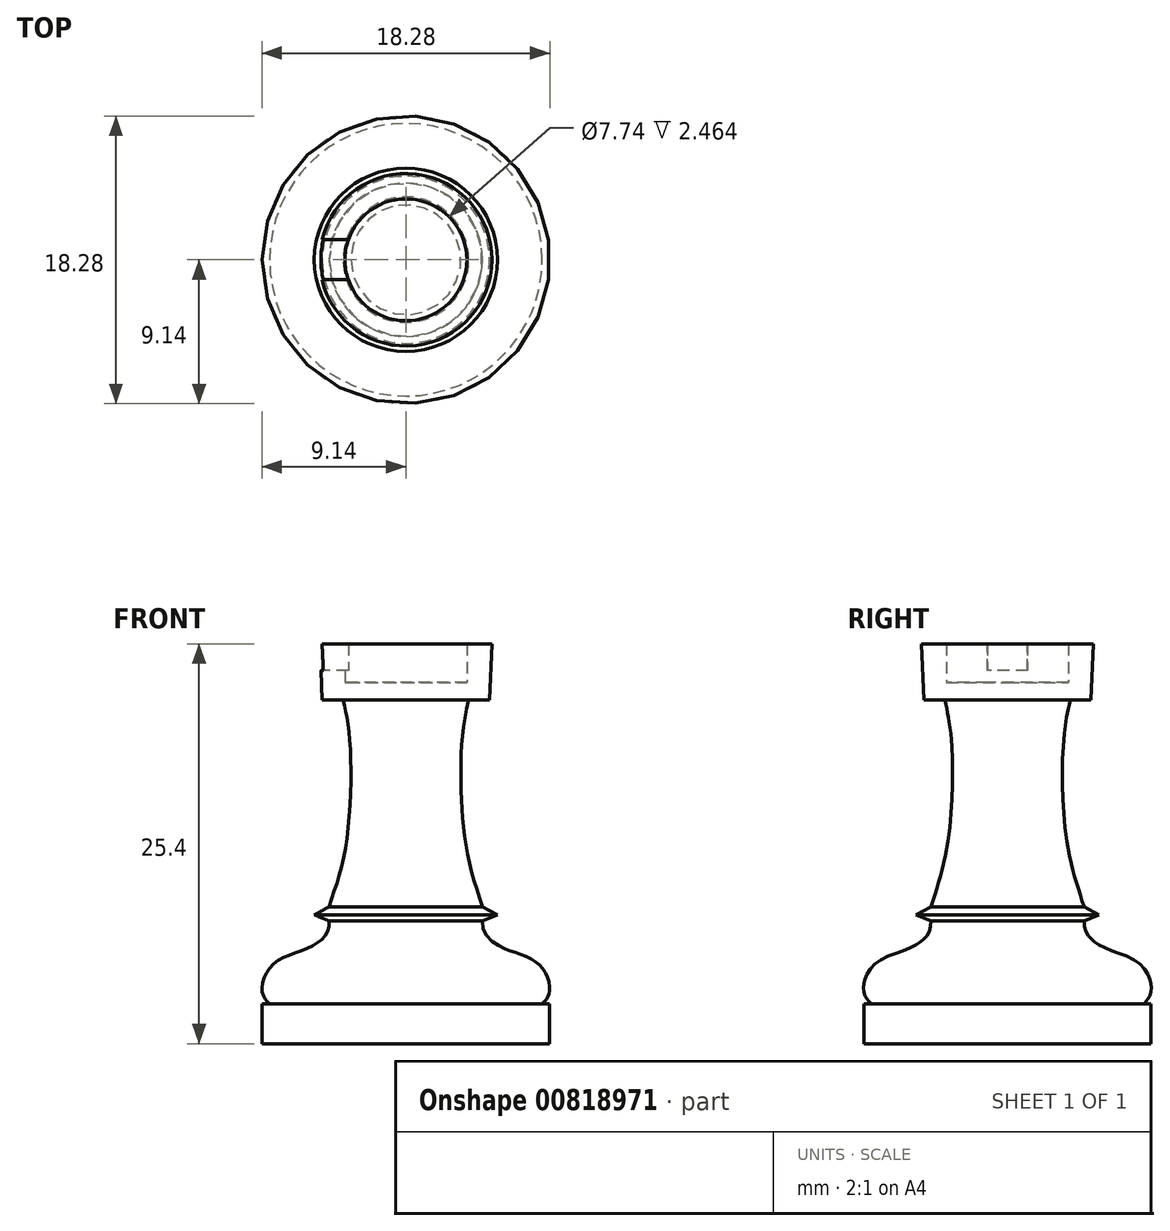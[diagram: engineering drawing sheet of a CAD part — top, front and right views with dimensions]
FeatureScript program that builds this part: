
annotation { "Feature Type Name" : "Feature", "Feature Type Description" : "" }
export const myFeature = defineFeature(function(context is Context, id is Id, definition is map)
    precondition{}
    {
        {
            var Q0;
            Q0=qCreatedBy(makeId("Front.planeOp"),FACE);
            var sketch = newSketch(context, id + "F0", { "sketchPlane" : qUnion([Q0])});
            skLineSegment(sketch, "E0", {"start": v(0, 0) * mm, "end": v(9.12, 0) * mm});
            skLineSegment(sketch, "E1", {"start": v(0, 0) * mm, "end": v(0, 25.4) * mm});
            skLineSegment(sketch, "E2", {"start": v(9.12, 0) * mm, "end": v(9.12, 2.54) * mm});
            skLineSegment(sketch, "E3", {"start": v(9.12, 2.54) * mm, "end": v(0, 2.54) * mm});
            skPoint(sketch, "E4.1.internal.snap0", {"position": v(9.12, 1.27) * mm});
            skFitSpline(sketch, "E4", {"points": [v(8.66, 2.54) * mm, v(9.12, 3.28) * mm, v(8.44, 5.04) * mm, v(5.9, 6.22) * mm, v(4.87, 7.8) * mm], "startDerivative": vector(3.43, 3.44) * mm, "endDerivative": vector(0.6, 8.31) * mm});
            skLineSegment(sketch, "E5", {"start": v(4.87, 7.8) * mm, "end": v(5.82, 8.18) * mm});
            skLineSegment(sketch, "E6", {"start": v(5.82, 8.18) * mm, "end": v(4.87, 8.7) * mm});
            skLineSegment(sketch, "E7", {"start": v(4.87, 8.7) * mm, "end": v(0, 8.7) * mm});
            skLineSegment(sketch, "E8", {"start": v(4.87, 21.83) * mm, "end": v(5.31, 21.83) * mm});
            skLineSegment(sketch, "E9", {"start": v(0, 25.4) * mm, "end": v(5.47, 25.4) * mm});
            skLineSegment(sketch, "E10", {"start": v(5.47, 25.4) * mm, "end": v(5.31, 21.83) * mm});
            skFitSpline(sketch, "E11", {"points": [v(4.87, 8.7) * mm, v(3.78, 12.8) * mm, v(3.57, 19.35) * mm, v(3.99, 21.83) * mm], "startDerivative": vector(-3.75, 11.49) * mm, "endDerivative": vector(1.93, 8.3) * mm});
            skLineSegment(sketch, "E12", {"start": v(4.87, 21.83) * mm, "end": v(3.99, 21.83) * mm});
            skPoint(sketch, "E13.endSnap0", {"position": v(4.43, 21.83) * mm});
            skSolve(sketch);
        }
        {
            var Q0;
            Q0 = qSketchRegion(id + "F0", true);
            var Q1;
            Q1=sQuery(id+"F0.wireOp",EDGE,"E1");
            revolve(context, id + "F1", {"surfaceOperationType" : NewSurfaceOperationType.NEW, "entities" : qUnion([Q0]), "axis" : qUnion([Q1]), "revolveType" : RevolveType.FULL});
        }
        {
            var Q0;
            Q0=makeQuery(id+"F1.opRevolve","SWEPT_FACE",FACE,{"disambiguationData":[OSD([sQuery(id+"F0.wireOp",EDGE,"E9")])]});
            var sketch = newSketch(context, id + "F2", { "sketchPlane" : qUnion([Q0])});
            skLineSegment(sketch, "E14.bottom", {"start": v(1.27, 1.27) * mm, "end": v(-1.27, 1.27) * mm});
            skLineSegment(sketch, "E14.top", {"start": v(1.27, -1.27) * mm, "end": v(-1.27, -1.27) * mm});
            skLineSegment(sketch, "E14.left", {"start": v(1.27, 1.27) * mm, "end": v(1.27, -1.27) * mm});
            skLineSegment(sketch, "E14.right", {"start": v(-1.27, 1.27) * mm, "end": v(-1.27, -1.27) * mm});
            skPoint(sketch, "E14.middle", {"position": v(0, 0) * mm});
            skLineSegment(sketch, "E15.bottom", {"start": v(-1.27, 1.27) * mm, "end": v(1.27, 1.27) * mm});
            skLineSegment(sketch, "E15.top", {"start": v(-1.27, 6.9) * mm, "end": v(1.27, 6.9) * mm});
            skLineSegment(sketch, "E15.left", {"start": v(-1.27, 1.27) * mm, "end": v(-1.27, 6.9) * mm});
            skLineSegment(sketch, "E15.right", {"start": v(1.27, 1.27) * mm, "end": v(1.27, 6.9) * mm});
            skLineSegment(sketch, "E16.1.0", {"start": v(-1.27, 1.27) * mm, "end": v(-6.9, 1.27) * mm});
            skLineSegment(sketch, "E16.1.1", {"start": v(-1.27, -1.27) * mm, "end": v(-1.27, 1.27) * mm});
            skLineSegment(sketch, "E16.1.2", {"start": v(-6.9, -1.27) * mm, "end": v(-6.9, 1.27) * mm});
            skLineSegment(sketch, "E16.1.3", {"start": v(-1.27, -1.27) * mm, "end": v(-6.9, -1.27) * mm});
            skLineSegment(sketch, "E16.2.0", {"start": v(-1.27, -1.27) * mm, "end": v(-1.27, -6.9) * mm});
            skLineSegment(sketch, "E16.2.2", {"start": v(1.27, -6.9) * mm, "end": v(-1.27, -6.9) * mm});
            skLineSegment(sketch, "E16.2.3", {"start": v(1.27, -1.27) * mm, "end": v(1.27, -6.9) * mm});
            skLineSegment(sketch, "E16.2.4", {"start": v(-1.27, -1.27) * mm, "end": v(1.27, -1.27) * mm});
            skLineSegment(sketch, "E16.3.0", {"start": v(1.27, -1.27) * mm, "end": v(6.9, -1.27) * mm});
            skLineSegment(sketch, "E16.3.2", {"start": v(6.9, 1.27) * mm, "end": v(6.9, -1.27) * mm});
            skLineSegment(sketch, "E16.3.3", {"start": v(1.27, 1.27) * mm, "end": v(6.9, 1.27) * mm});
            skLineSegment(sketch, "E16.3.4", {"start": v(1.27, -1.27) * mm, "end": v(1.27, 1.27) * mm});
            skSolve(sketch);
        }
        {
            var Q0;
            {var subQ0=sQuery(id+"F2.wireOp",EDGE,"E14.right");Q0=makeQuery(id+"F2.imprint","IMPRINT",FACE,{"disambiguationData":[TD([[makeQuery(id+"F2.imprint","IMPRINT",EDGE,{"derivedFrom":subQ0}),-1.0]])]});}
            var Q1;
            {var subQ0=sQuery(id+"F2.wireOp",EDGE,"E16.3.4");Q1=makeQuery(id+"F2.imprint","IMPRINT",FACE,{"disambiguationData":[TD([[makeQuery(id+"F2.imprint","IMPRINT",EDGE,{"derivedFrom":subQ0}),-1.0]])]});}
            var Q2;
            {var subQ0=sQuery(id+"F2.wireOp",EDGE,"E16.2.4");Q2=makeQuery(id+"F2.imprint","IMPRINT",FACE,{"disambiguationData":[TD([[makeQuery(id+"F2.imprint","IMPRINT",EDGE,{"derivedFrom":subQ0}),-1.0]])]});}
            var Q3;
            {var subQ0=sQuery(id+"F2.wireOp",EDGE,"E15.bottom");Q3=makeQuery(id+"F2.imprint","IMPRINT",FACE,{"disambiguationData":[TD([[makeQuery(id+"F2.imprint","IMPRINT",EDGE,{"derivedFrom":subQ0}),1.0]])]});}
            var Q4;
            Q4=makeQuery(id+"F2.imprint","IMPRINT",FACE,{"disambiguationData":[TD([[makeQuery(id+"F2.imprint","IMPRINT",EDGE,{"derivedFrom":sQuery(id+"F2.wireOp",EDGE,"E15.bottom")}),-1.0]])]});
            extrude(context, id + "F3", {"entities" : qUnion([Q0, Q1, Q2, Q3, Q4]), "operationType" : NewBodyOperationType.REMOVE, "oppositeDirection" : true, "depth" : 1.7 * mm, "offsetDistance" : 25.4 * mm});
        }
        {
            var Q0;
            Q0=makeQuery(id+"F3.boolean.opBoolean","COPY",FACE,{"derivedFrom":makeQuery(id+"F3.opExtrude","CAP_FACE",FACE,{"disambiguationData":[OSD([sQuery(id+"F0.wireOp",EDGE,"E9"),sQuery(id+"F0.wireOp",EDGE,"E10"),sQuery(id+"F2.wireOp",EDGE,"E15.left"),sQuery(id+"F2.wireOp",EDGE,"E15.right"),sQuery(id+"F2.wireOp",EDGE,"E16.1.0"),sQuery(id+"F2.wireOp",EDGE,"E16.1.3"),sQuery(id+"F2.wireOp",EDGE,"E16.2.0"),sQuery(id+"F2.wireOp",EDGE,"E16.2.3"),sQuery(id+"F2.wireOp",EDGE,"E16.3.0"),sQuery(id+"F2.wireOp",EDGE,"E16.3.3")])],"isStart":false})});
            var sketch = newSketch(context, id + "F4", { "sketchPlane" : qUnion([Q0])});
            skCircle(sketch, "E17", {"center": v(0, 0) * mm, "radius": 3.87 * mm});
            skSolve(sketch);
        }
        {
            var Q0;
            Q0 = qSketchRegion(id + "F4", true);
            extrude(context, id + "F5", {"entities" : qUnion([Q0]), "operationType" : NewBodyOperationType.REMOVE, "depth" : 25.4 * mm, "offsetDistance" : 25.4 * mm});
        }
        {
            var Q0;
            Q0 = qSketchRegion(id + "F4", true);
            extrude(context, id + "F6", {"entities" : qUnion([Q0]), "operationType" : NewBodyOperationType.REMOVE, "oppositeDirection" : true, "depth" : 0.76 * mm, "offsetDistance" : 25.4 * mm});
        }
    });
